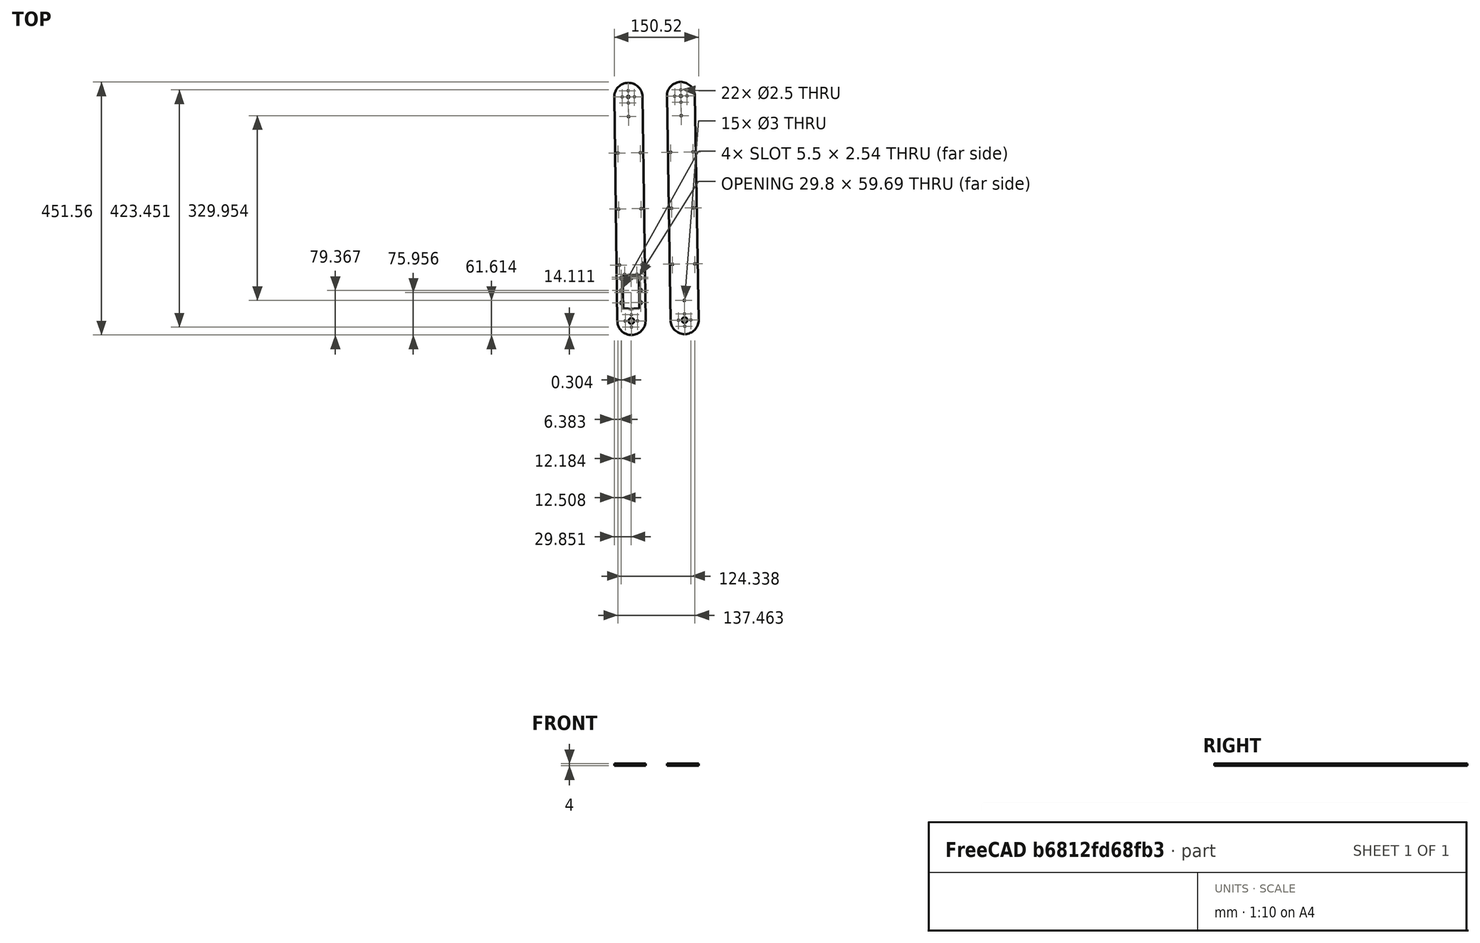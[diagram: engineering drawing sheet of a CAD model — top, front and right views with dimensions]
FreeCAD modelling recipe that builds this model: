
FCSTD DOCUMENT  (FreeCAD 1.0R39109 (Git))
Label: arm_assembly_def2
License: All rights reserved
LicenseURL: https://en.wikipedia.org/wiki/All_rights_reserved
objects: Sketcher::SketchObject×2, PartDesign::Pad×2, PartDesign::Body×2, Assembly::JointGroup×1, Assembly::AssemblyObject×1
note: 12 computed .brp shape members not serialized (recipe doc carries the construction recipe); baked Part::Feature solids carry a one-line shape summary decoded from their .brp

FEATURE [Sketcher::SketchObject] Sketch
  ArcFitTolerance = 1e-06
  AttachmentSupport = -> [XY_Plane]
  FullyConstrained = false
  MakeInternals = false
  MapMode = 5
  sketch-geometry (101):
    g0: LineSegment [constr] StartX=1.5008e-12 StartY=20 StartZ=0 EndX=1.5008e-12 EndY=-20 EndZ=0
    g1: LineSegment [constr] StartX=0 StartY=0 StartZ=0 EndX=0 EndY=400 EndZ=0
    g2: LineSegment [constr] StartX=1.5008e-12 StartY=20 StartZ=0 EndX=1.5008e-12 EndY=25 EndZ=0
    g3: Circle CenterX=0 CenterY=400 CenterZ=0 NormalX=0 NormalY=0 NormalZ=1 AngleXU=0 Radius=2
    g4: Circle CenterX=-10.9997 CenterY=400 CenterZ=0 NormalX=0 NormalY=0 NormalZ=1 AngleXU=0 Radius=1.25
    g5: Circle CenterX=0 CenterY=389 CenterZ=0 NormalX=0 NormalY=0 NormalZ=1 AngleXU=0 Radius=1.25
    g6: Circle CenterX=10.9997 CenterY=400 CenterZ=0 NormalX=0 NormalY=0 NormalZ=1 AngleXU=0 Radius=1.25
    g7: Circle CenterX=0 CenterY=411 CenterZ=0 NormalX=0 NormalY=0 NormalZ=1 AngleXU=0 Radius=1.25
    g8: LineSegment [constr] StartX=0 StartY=-5 StartZ=0 EndX=0 EndY=5.99996 EndZ=0
    g9: Circle [constr] CenterX=0 CenterY=0 CenterZ=0 NormalX=0 NormalY=0 NormalZ=1 AngleXU=0 Radius=14
    g10: LineSegment [constr] StartX=0 StartY=0 StartZ=0 EndX=25.23 EndY=0 EndZ=0
    g11: Circle [constr] CenterX=0 CenterY=-3.8e-05 CenterZ=0 NormalX=0 NormalY=0 NormalZ=1 AngleXU=0 Radius=11
    g12: Circle CenterX=0 CenterY=0 CenterZ=0 NormalX=0 NormalY=0 NormalZ=1 AngleXU=0 Radius=5
    g13: Circle CenterX=10.9997 CenterY=0 CenterZ=0 NormalX=0 NormalY=0 NormalZ=1 AngleXU=0 Radius=1.25
    g14: Circle CenterX=-10.9997 CenterY=0 CenterZ=0 NormalX=0 NormalY=0 NormalZ=1 AngleXU=0 Radius=1.25
    g15: Circle CenterX=0 CenterY=-10.9997 CenterZ=0 NormalX=0 NormalY=0 NormalZ=1 AngleXU=0 Radius=1.25
    g16: Circle CenterX=0 CenterY=11 CenterZ=0 NormalX=0 NormalY=0 NormalZ=1 AngleXU=0 Radius=1.25
    g17: LineSegment [constr] StartX=0 StartY=0 StartZ=0 EndX=-25 EndY=0 EndZ=0
    g18: LineSegment [constr] StartX=20.1368 StartY=86.1 StartZ=0 EndX=20.1368 EndY=25 EndZ=0
    g19: LineSegment [constr] StartX=0.036848 StartY=80.5 StartZ=0 EndX=14.5368 EndY=80.5 EndZ=0
    g20: LineSegment StartX=14.5368 StartY=80.5 StartZ=0 EndX=-14.4632 EndY=80.5 EndZ=0
    g21: LineSegment StartX=14.5368 StartY=80.5 StartZ=0 EndX=14.5368 EndY=25 EndZ=0
    g22: Circle CenterX=11.0368 CenterY=83.3 CenterZ=0 NormalX=0 NormalY=0 NormalZ=1 AngleXU=0 Radius=1.25
    g23: Circle CenterX=17.3368 CenterY=78 CenterZ=0 NormalX=0 NormalY=0 NormalZ=1 AngleXU=0 Radius=1.25
    g24: LineSegment [constr] StartX=-20.0632 StartY=86.1 StartZ=0 EndX=20.1368 EndY=86.1 EndZ=0
    g25: Circle [constr] CenterX=17.3368 CenterY=56.0002 CenterZ=0 NormalX=0 NormalY=0 NormalZ=1 AngleXU=0 Radius=1.25
    g26: Circle [constr] CenterX=17.3368 CenterY=34 CenterZ=0 NormalX=0 NormalY=0 NormalZ=1 AngleXU=0 Radius=1.25
    g27: Circle [constr] CenterX=0.036848 CenterY=38 CenterZ=0 NormalX=0 NormalY=0 NormalZ=1 AngleXU=0 Radius=14
    g28: ArcOfCircle [constr] CenterX=0.036848 CenterY=38 CenterZ=0 NormalX=0 NormalY=0 NormalZ=1 AngleXU=0 Radius=14 StartAngle=4.33214 EndAngle=5.09264
    g29: LineSegment [constr] StartX=5.233 StartY=25 StartZ=0 EndX=14.5368 EndY=25 EndZ=0
    g30: LineSegment [constr] StartX=14.5368 StartY=25 StartZ=0 EndX=20.1368 EndY=25 EndZ=0
    g31: LineSegment [constr] StartX=17.3368 StartY=56.0002 StartZ=0 EndX=-17.2632 EndY=56.0002 EndZ=0
    g32: LineSegment [constr] StartX=-20.0632 StartY=25 StartZ=0 EndX=-20.0632 EndY=86.1 EndZ=0
    g33: LineSegment StartX=-14.4632 StartY=80.5 StartZ=0 EndX=-14.4632 EndY=25 EndZ=0
    g34: Circle CenterX=-17.2632 CenterY=78 CenterZ=0 NormalX=0 NormalY=0 NormalZ=1 AngleXU=0 Radius=1.25
    g35: Circle CenterX=-10.9632 CenterY=83.3 CenterZ=0 NormalX=0 NormalY=0 NormalZ=1 AngleXU=0 Radius=1.25
    g36: Circle [constr] CenterX=-17.2632 CenterY=56.0002 CenterZ=0 NormalX=0 NormalY=0 NormalZ=1 AngleXU=0 Radius=1.25
    g37: Circle [constr] CenterX=-17.2632 CenterY=34 CenterZ=0 NormalX=0 NormalY=0 NormalZ=1 AngleXU=0 Radius=1.25
    g38: LineSegment [constr] StartX=-14.4632 StartY=25 StartZ=0 EndX=-5.15931 EndY=25 EndZ=0
    g39: LineSegment [constr] StartX=-20.0632 StartY=25 StartZ=0 EndX=-14.4632 EndY=25 EndZ=0
    g40: ArcOfCircle CenterX=0.115002 CenterY=3.75548e-06 CenterZ=0 NormalX=0 NormalY=0 NormalZ=1 AngleXU=0 Radius=25.115 StartAngle=3.14159 EndAngle=6.28319
    g41: ArcOfCircle CenterX=0.115002 CenterY=399.959 CenterZ=0 NormalX=0 NormalY=0 NormalZ=1 AngleXU=0 Radius=25.115 StartAngle=0 EndAngle=3.14159
    g42: LineSegment StartX=-25 StartY=3.75548e-06 StartZ=0 EndX=-25 EndY=399.959 EndZ=0
    g43: LineSegment StartX=25.23 StartY=3.75548e-06 StartZ=0 EndX=25.23 EndY=399.959 EndZ=0
    g44: LineSegment [constr] StartX=25.23 StartY=199.98 StartZ=0 EndX=-25 EndY=199.98 EndZ=0
    g45: LineSegment [constr] StartX=25.23 StartY=199.98 StartZ=0 EndX=55.23 EndY=199.98 EndZ=0
    g46: LineSegment [constr] StartX=25.23 StartY=0 StartZ=0 EndX=55.23 EndY=0 EndZ=0
    g47: LineSegment [constr] StartX=55.23 StartY=0 StartZ=0 EndX=55.23 EndY=199.98 EndZ=0
    g48: LineSegment [constr] StartX=55.23 StartY=99.9898 StartZ=0 EndX=25.23 EndY=99.9898 EndZ=0
    g49: LineSegment [constr] StartX=25.23 StartY=99.9898 StartZ=0 EndX=-25 EndY=99.9898 EndZ=0
    g50: LineSegment [constr] StartX=25.23 StartY=399.959 StartZ=0 EndX=55.23 EndY=399.959 EndZ=0
    g51: LineSegment [constr] StartX=55.23 StartY=399.959 StartZ=0 EndX=55.23 EndY=199.98 EndZ=0
    g52: LineSegment [constr] StartX=55.23 StartY=299.969 StartZ=0 EndX=25.23 EndY=299.969 EndZ=0
    g53: LineSegment [constr] StartX=25.23 StartY=299.969 StartZ=0 EndX=-25 EndY=299.969 EndZ=0
    g54: LineSegment [constr] StartX=-25 StartY=299.969 StartZ=0 EndX=-20 EndY=299.969 EndZ=0
    g55: LineSegment [constr] StartX=-20 StartY=299.969 StartZ=0 EndX=-20 EndY=199.98 EndZ=0
    g56: LineSegment [constr] StartX=-20 StartY=199.98 StartZ=0 EndX=-20 EndY=99.9898 EndZ=0
    g57: LineSegment [constr] StartX=25.23 StartY=299.969 StartZ=0 EndX=20.23 EndY=299.969 EndZ=0
    g58: LineSegment [constr] StartX=20.23 StartY=299.969 StartZ=0 EndX=20.23 EndY=199.98 EndZ=0
    g59: LineSegment [constr] StartX=20.23 StartY=199.98 StartZ=0 EndX=20.23 EndY=99.9898 EndZ=0
    g60: Circle CenterX=-20 CenterY=299.969 CenterZ=0 NormalX=0 NormalY=0 NormalZ=1 AngleXU=0 Radius=1.5
    g61: Circle CenterX=20.23 CenterY=299.969 CenterZ=0 NormalX=0 NormalY=0 NormalZ=1 AngleXU=0 Radius=1.5
    g62: Circle CenterX=-20 CenterY=199.98 CenterZ=0 NormalX=0 NormalY=0 NormalZ=1 AngleXU=0 Radius=1.5
    g63: Circle CenterX=20.23 CenterY=199.98 CenterZ=0 NormalX=0 NormalY=0 NormalZ=1 AngleXU=0 Radius=1.5
    g64: Circle CenterX=-20 CenterY=99.9898 CenterZ=0 NormalX=0 NormalY=0 NormalZ=1 AngleXU=0 Radius=1.5
    g65: Circle CenterX=20.23 CenterY=99.9898 CenterZ=0 NormalX=0 NormalY=0 NormalZ=1 AngleXU=0 Radius=1.5
    g66: LineSegment [constr] StartX=-17.2632 StartY=34 StartZ=0 EndX=17.3368 EndY=34 EndZ=0
    g67: LineSegment [constr] StartX=-17.2632 StartY=34 StartZ=0 EndX=-17.2632 EndY=31 EndZ=0
    g68: LineSegment [constr] StartX=17.3368 StartY=34 StartZ=0 EndX=17.3368 EndY=31 EndZ=0
    g69: ArcOfCircle CenterX=-17.2632 CenterY=34 CenterZ=0 NormalX=0 NormalY=0 NormalZ=1 AngleXU=0 Radius=1.25 StartAngle=1.93e-14 EndAngle=3.14159
    g70: ArcOfCircle CenterX=-17.2632 CenterY=31 CenterZ=0 NormalX=0 NormalY=0 NormalZ=1 AngleXU=0 Radius=1.25 StartAngle=3.14159 EndAngle=6.28319
    g71: LineSegment StartX=-16.0132 StartY=34 StartZ=0 EndX=-16.0132 EndY=31 EndZ=0
    g72: LineSegment StartX=-18.5132 StartY=34 StartZ=0 EndX=-18.5132 EndY=31 EndZ=0
    g73: ArcOfCircle CenterX=17.3368 CenterY=34 CenterZ=0 NormalX=0 NormalY=0 NormalZ=1 AngleXU=0 Radius=1.25 StartAngle=1e-16 EndAngle=3.14159
    g74: ArcOfCircle CenterX=17.3368 CenterY=31 CenterZ=0 NormalX=0 NormalY=0 NormalZ=1 AngleXU=0 Radius=1.25 StartAngle=3.14159 EndAngle=6.28319
    g75: LineSegment StartX=18.5868 StartY=34 StartZ=0 EndX=18.5868 EndY=31 EndZ=0
    g76: LineSegment StartX=16.0868 StartY=34 StartZ=0 EndX=16.0868 EndY=31 EndZ=0
    g77: LineSegment [constr] StartX=-17.2632 StartY=78 StartZ=0 EndX=17.3368 EndY=78 EndZ=0
    g78: LineSegment [constr] StartX=-17.2632 StartY=78 StartZ=0 EndX=-17.2632 EndY=75 EndZ=0
    g79: Circle CenterX=-17.2632 CenterY=75 CenterZ=0 NormalX=0 NormalY=0 NormalZ=1 AngleXU=0 Radius=1.25
    g80: LineSegment [constr] StartX=17.3368 StartY=78 StartZ=0 EndX=17.3368 EndY=75 EndZ=0
    g81: Circle CenterX=17.3368 CenterY=75 CenterZ=0 NormalX=0 NormalY=0 NormalZ=1 AngleXU=0 Radius=1.25
    g82: LineSegment StartX=-14.4632 StartY=25 StartZ=0 EndX=-14.4632 EndY=22 EndZ=0
    g83: LineSegment StartX=14.5368 StartY=25 StartZ=0 EndX=14.5368 EndY=22 EndZ=0
    g84: LineSegment StartX=5.233 StartY=22 StartZ=0 EndX=14.5368 EndY=22 EndZ=0
    g85: ArcOfCircle CenterX=0.036848 CenterY=35 CenterZ=0 NormalX=0 NormalY=0 NormalZ=1 AngleXU=0 Radius=14 StartAngle=4.33214 EndAngle=5.09264
    g86: LineSegment StartX=-14.4632 StartY=22 StartZ=0 EndX=-5.15931 EndY=22 EndZ=0
    g87: LineSegment [constr] StartX=-17.2632 StartY=56.0002 StartZ=0 EndX=-17.2632 EndY=53.0002 EndZ=0
    g88: LineSegment [constr] StartX=17.3368 StartY=56.0002 StartZ=0 EndX=17.3368 EndY=53.0002 EndZ=0
    g89: ArcOfCircle CenterX=-17.2632 CenterY=56.0002 CenterZ=0 NormalX=0 NormalY=0 NormalZ=1 AngleXU=0 Radius=1.25 StartAngle=1.93e-14 EndAngle=3.14159
    g90: ArcOfCircle CenterX=-17.2632 CenterY=53.0002 CenterZ=0 NormalX=0 NormalY=0 NormalZ=1 AngleXU=0 Radius=1.25 StartAngle=3.14159 EndAngle=6.28319
    g91: LineSegment StartX=-16.0132 StartY=56.0002 StartZ=0 EndX=-16.0132 EndY=53.0002 EndZ=0
    g92: LineSegment StartX=-18.5132 StartY=56.0002 StartZ=0 EndX=-18.5132 EndY=53.0002 EndZ=0
    g93: ArcOfCircle CenterX=17.3368 CenterY=56.0002 CenterZ=0 NormalX=0 NormalY=0 NormalZ=1 AngleXU=0 Radius=1.25 StartAngle=2.46e-14 EndAngle=3.14159
    g94: ArcOfCircle CenterX=17.3368 CenterY=53.0002 CenterZ=0 NormalX=0 NormalY=0 NormalZ=1 AngleXU=0 Radius=1.25 StartAngle=3.14159 EndAngle=6.28319
    g95: LineSegment StartX=18.5868 StartY=56.0002 StartZ=0 EndX=18.5868 EndY=53.0002 EndZ=0
    g96: LineSegment StartX=16.0868 StartY=56.0002 StartZ=0 EndX=16.0868 EndY=53.0002 EndZ=0
    g97: Circle [constr] CenterX=0.115002 CenterY=399.959 CenterZ=0 NormalX=0 NormalY=0 NormalZ=1 AngleXU=0 Radius=25.115
    g98: LineSegment [constr] StartX=0 StartY=400 StartZ=0 EndX=0 EndY=374.844 EndZ=0
    g99: LineSegment [constr] StartX=0 StartY=374.844 StartZ=0 EndX=0 EndY=364.844 EndZ=0
    g100: Circle CenterX=0 CenterY=364.844 CenterZ=0 NormalX=0 NormalY=0 NormalZ=1 AngleXU=0 Radius=1.5
  constraints (211):
    c: Vertical(g0)
    c: Vertical(g1)
    c: Coincident(g2,g0)
    c: Vertical(g2)
    c: Diameter(g3) = 4
    c: Coincident(g3,g1)
    c: Diameter(g7) = 2.5
    c: Diameter(g4) = 2.5
    c: Diameter(g5) = 2.5
    c: Diameter(g6) = 2.5
    c: Vertical(g8)
    c: Diameter(g9) = 28
    c: Coincident(g17,g9)
    c: Horizontal(g17)
    c: Coincident(g10,g9)
    c: Horizontal(g10)
    c: Diameter(g11) = 22
    c: Diameter(g12) = 10
    c: Coincident(g12,g9)
    c: Diameter(g16) = 2.5
    c: Diameter(g14) = 2.5
    c: Diameter(g15) = 2.5
    c: Diameter(g13) = 2.5
    c: Coincident(g24,g18)
    c: Coincident(g32,g24)
    c: Horizontal(g24)
    c: Vertical(g18)
    c: Vertical(g32)
    c: Distance(g18,g32) = 40.2
    c: Distance(g24,g32) = 61.1
    c: Diameter(g28) = 28
    c: Horizontal(g19)
    c: Coincident(g20,g19)
    c: Horizontal(g20)
    c: Coincident(g33,g20)
    c: Vertical(g33)
    c: Coincident(g21,g19)
    c: Vertical(g21)
    c: Diameter(g22) = 2.5
    c: Equal(g22,g35)
    c: Equal(g22,g26)
    c: Equal(g22,g37)
    c: Equal(g22,g36)
    c: Equal(g22,g34)
    c: Equal(g22,g23)
    c: Equal(g22,g25)
    c: Coincident(g27,g28)
    c: PointOnObject(g28,g27)
    c: Coincident(g29,g28)
    c: Coincident(g29,g21)
    c: Horizontal(g29)
    c: Coincident(g30,g21)
    c: Coincident(g30,g18)
    c: Horizontal(g30)
    c: Coincident(g38,g33)
    c: Coincident(g38,g28)
    c: Horizontal(g38)
    c: Coincident(g39,g32)
    c: Coincident(g39,g33)
    c: Horizontal(g39)
    c: Coincident(g31,g25)
    c: Coincident(g31,g36)
    c: Horizontal(g31)
    c: DistanceY(g27,g1) = 362
    c: Tangent(g40,g42) = 1.5708
    c: Tangent(g40,g43) = -1.5708
    c: Tangent(g41,g42) = 1.5708
    c: Tangent(g41,g43) = -1.5708
    c: Equal(g40,g41)
    c: Symmetric(g43,g43,g44)
    c: Symmetric(g42,g42,g44)
    c: Horizontal(g44)
    c: Distance(g45) = 30
    c: Horizontal(g45)
    c: Coincident(g45,g44)
    c: Distance(g46) = 30
    c: Horizontal(g46)
    c: Coincident(g46,g10)
    c: PointOnObject(g46,g-1)
    c: Coincident(g47,g46)
    c: Coincident(g47,g45)
    c: Vertical(g47)
    c: Symmetric(g47,g47,g48)
    c: PointOnObject(g48,g43)
    c: Horizontal(g48)
    c: Coincident(g49,g48)
    c: PointOnObject(g49,g42)
    c: Horizontal(g49)
    c: Distance(g50) = 30
    c: Horizontal(g50)
    c: Coincident(g50,g41)
    c: Coincident(g51,g50)
    c: Coincident(g51,g45)
    c: Symmetric(g51,g51,g52)
    c: PointOnObject(g52,g43)
    c: Horizontal(g52)
    c: Coincident(g53,g52)
    c: PointOnObject(g53,g42)
    c: Horizontal(g53)
    c: Distance(g54) = 5
    c: Coincident(g54,g53)
    c: PointOnObject(g54,g53)
    c: Coincident(g55,g54)
    c: PointOnObject(g55,g44)
    c: Vertical(g55)
    c: Coincident(g56,g55)
    c: PointOnObject(g56,g49)
    c: Vertical(g56)
    c: Distance(g57) = 5
    c: Coincident(g57,g52)
    c: PointOnObject(g57,g53)
    c: Coincident(g58,g57)
    c: PointOnObject(g58,g44)
    c: Vertical(g58)
    c: Coincident(g59,g58)
    c: PointOnObject(g59,g49)
    c: Vertical(g59)
    c: Coincident(g60,g54)
    c: Diameter(g60) = 3
    c: Coincident(g61,g57)
    c: Equal(g60,g61)
    c: Coincident(g62,g55)
    c: Equal(g60,g62)
    c: Coincident(g63,g58)
    c: Equal(g62,g63)
    c: Coincident(g64,g56)
    c: Equal(g62,g64)
    c: Coincident(g65,g59)
    c: Equal(g64,g65)
    c: DistanceY(g40,g27) = 38
    c: Coincident(g66,g37)
    c: Coincident(g66,g26)
    c: Horizontal(g66)
    c: DistanceX(g66,g66) = 34.6
    c: Distance(g67) = 3
    c: Coincident(g67,g37)
    c: Vertical(g67)
    c: Distance(g68) = 3
    c: Coincident(g68,g26)
    c: Vertical(g68)
    c: Tangent(g69,g71) = 1.5708
    c: Tangent(g69,g72) = -1.5708
    c: Tangent(g70,g71) = 1.5708
    c: Tangent(g70,g72) = -1.5708
    c: Equal(g69,g70)
    c: Radius(g69) = 1.25
    c: Coincident(g69,g37)
    c: Coincident(g70,g67)
    c: Tangent(g73,g75) = 1.5708
    c: Tangent(g73,g76) = -1.5708
    c: Tangent(g74,g75) = 1.5708
    c: Tangent(g74,g76) = -1.5708
    c: Equal(g73,g74)
    c: Coincident(g77,g34)
    c: Coincident(g77,g23)
    c: Horizontal(g77)
    c: DistanceX(g77,g77) = 34.6
    c: Distance(g78) = 3
    c: Coincident(g78,g34)
    c: Vertical(g78)
    c: Coincident(g79,g78)
    c: Equal(g79,g34)
    c: Distance(g80) = 3
    c: Coincident(g80,g23)
    c: Vertical(g80)
    c: Coincident(g81,g80)
    c: Equal(g81,g23)
    c: DistanceX(g33,g21) = 29
    c: Distance(g82) = 3
    c: Coincident(g82,g33)
    c: Vertical(g82)
    c: Distance(g83) = 3
    c: Coincident(g83,g21)
    c: Vertical(g83)
    c: Diameter(g85) = 28
    c: Coincident(g84,g85)
    c: Horizontal(g84)
    c: Coincident(g86,g85)
    c: Horizontal(g86)
    c: DistanceX(g31,g31) = 34.6
    c: Distance(g87) = 3
    c: Coincident(g87,g31)
    c: Vertical(g87)
    c: Distance(g88) = 3
    c: Coincident(g88,g25)
    c: Vertical(g88)
    c: Tangent(g89,g91) = 1.5708
    c: Tangent(g89,g92) = -1.5708
    c: Tangent(g90,g91) = 1.5708
    c: Tangent(g90,g92) = -1.5708
    c: Equal(g89,g90)
    c: Radius(g89) = 1.25
    c: Coincident(g89,g31)
    c: Coincident(g90,g87)
    c: Tangent(g93,g95) = 1.5708
    c: Tangent(g93,g96) = -1.5708
    c: Tangent(g94,g95) = 1.5708
    c: Tangent(g94,g96) = -1.5708
    c: Equal(g93,g94)
    c: Coincident(g97,g41)
    c: PointOnObject(g41,g97)
    c: DistanceX(g1) = 0
    c: DistanceY(g1) = 400
    c: Coincident(g98,g1)
    c: PointOnObject(g98,g97)
    c: Vertical(g98)
    c: Distance(g99) = 10
    c: Coincident(g99,g98)
    c: PointOnObject(g99,g1)
    c: Diameter(g100) = 3
    c: Coincident(g100,g99)
FEATURE [Sketcher::SketchObject] Sketch001
  ArcFitTolerance = 1e-06
  FullyConstrained = false
  MakeInternals = false
  MapMode = 5
  sketch-geometry (47):
    g0: Circle [constr] CenterX=0 CenterY=0.000303 CenterZ=0 NormalX=0 NormalY=0 NormalZ=1 AngleXU=0 Radius=14
    g1: LineSegment [constr] StartX=0 StartY=0.000303 StartZ=0 EndX=0 EndY=400.001 EndZ=0
    g2: Circle CenterX=0 CenterY=400.001 CenterZ=0 NormalX=0 NormalY=0 NormalZ=1 AngleXU=0 Radius=5
    g3: Circle CenterX=0 CenterY=0.000303 CenterZ=0 NormalX=0 NormalY=0 NormalZ=1 AngleXU=0 Radius=2
    g4: Circle [constr] CenterX=0 CenterY=0 CenterZ=0 NormalX=0 NormalY=0 NormalZ=1 AngleXU=0 Radius=11
    g5: ArcOfCircle CenterX=0 CenterY=0 CenterZ=0 NormalX=0 NormalY=0 NormalZ=1 AngleXU=0 Radius=25 StartAngle=3.14159 EndAngle=6.28319
    g6: ArcOfCircle CenterX=0 CenterY=400.001 CenterZ=0 NormalX=0 NormalY=0 NormalZ=1 AngleXU=0 Radius=25 StartAngle=6e-16 EndAngle=3.14159
    g7: LineSegment StartX=-25 StartY=-8e-15 StartZ=0 EndX=-25 EndY=400.001 EndZ=0
    g8: LineSegment StartX=25 StartY=0 StartZ=0 EndX=25 EndY=400.001 EndZ=0
    g9: Circle CenterX=10.9997 CenterY=400.001 CenterZ=0 NormalX=0 NormalY=0 NormalZ=1 AngleXU=0 Radius=1.25
    g10: Circle CenterX=0 CenterY=411.001 CenterZ=0 NormalX=0 NormalY=0 NormalZ=1 AngleXU=0 Radius=1.25
    g11: Circle CenterX=-10.9997 CenterY=400.001 CenterZ=0 NormalX=0 NormalY=0 NormalZ=1 AngleXU=0 Radius=1.25
    g12: Circle CenterX=0 CenterY=389.001 CenterZ=0 NormalX=0 NormalY=0 NormalZ=1 AngleXU=0 Radius=1.25
    g13: Circle CenterX=10.9997 CenterY=0.000303 CenterZ=0 NormalX=0 NormalY=0 NormalZ=1 AngleXU=0 Radius=1.25
    g14: Circle CenterX=0 CenterY=11 CenterZ=0 NormalX=0 NormalY=0 NormalZ=1 AngleXU=0 Radius=1.25
    g15: Circle CenterX=-10.9997 CenterY=0.000303 CenterZ=0 NormalX=0 NormalY=0 NormalZ=1 AngleXU=0 Radius=1.25
    g16: Circle CenterX=0 CenterY=-10.9994 CenterZ=0 NormalX=0 NormalY=0 NormalZ=1 AngleXU=0 Radius=1.25
    g17: LineSegment [constr] StartX=25 StartY=200 StartZ=0 EndX=-25 EndY=200 EndZ=0
    g18: LineSegment [constr] StartX=25 StartY=200 StartZ=0 EndX=55 EndY=200 EndZ=0
    g19: LineSegment [constr] StartX=25 StartY=0 StartZ=0 EndX=55 EndY=0 EndZ=0
    g20: LineSegment [constr] StartX=25 StartY=400.001 StartZ=0 EndX=55 EndY=400.001 EndZ=0
    g21: LineSegment [constr] StartX=55 StartY=200 StartZ=0 EndX=55 EndY=400.001 EndZ=0
    g22: LineSegment [constr] StartX=55 StartY=200 StartZ=0 EndX=55 EndY=0 EndZ=0
    g23: LineSegment [constr] StartX=55 StartY=100 StartZ=0 EndX=25 EndY=100 EndZ=0
    g24: LineSegment [constr] StartX=25 StartY=100 StartZ=0 EndX=-25 EndY=100 EndZ=0
    g25: LineSegment [constr] StartX=55 StartY=300 StartZ=0 EndX=25 EndY=300 EndZ=0
    g26: LineSegment [constr] StartX=25 StartY=300 StartZ=0 EndX=-25 EndY=300 EndZ=0
    g27: LineSegment [constr] StartX=-25 StartY=300 StartZ=0 EndX=-20 EndY=300 EndZ=0
    g28: LineSegment [constr] StartX=-20 StartY=300 StartZ=0 EndX=-20 EndY=200 EndZ=0
    g29: LineSegment [constr] StartX=-20 StartY=200 StartZ=0 EndX=-20 EndY=100 EndZ=0
    g30: LineSegment [constr] StartX=25 StartY=100 StartZ=0 EndX=20 EndY=100 EndZ=0
    g31: LineSegment [constr] StartX=20 StartY=100 StartZ=0 EndX=20 EndY=200 EndZ=0
    g32: LineSegment [constr] StartX=20 StartY=200 StartZ=0 EndX=20 EndY=300 EndZ=0
    g33: Circle CenterX=-20 CenterY=300 CenterZ=0 NormalX=0 NormalY=0 NormalZ=1 AngleXU=0 Radius=1.5
    g34: Circle CenterX=20 CenterY=300 CenterZ=0 NormalX=0 NormalY=0 NormalZ=1 AngleXU=0 Radius=1.5
    g35: Circle CenterX=-20 CenterY=200 CenterZ=0 NormalX=0 NormalY=0 NormalZ=1 AngleXU=0 Radius=1.5
    g36: Circle CenterX=20 CenterY=200 CenterZ=0 NormalX=0 NormalY=0 NormalZ=1 AngleXU=0 Radius=1.5
    g37: Circle CenterX=-20 CenterY=100 CenterZ=0 NormalX=0 NormalY=0 NormalZ=1 AngleXU=0 Radius=1.5
    g38: Circle CenterX=20 CenterY=100 CenterZ=0 NormalX=0 NormalY=0 NormalZ=1 AngleXU=0 Radius=1.5
    g39: Circle [constr] CenterX=0 CenterY=400.001 CenterZ=0 NormalX=0 NormalY=0 NormalZ=1 AngleXU=0 Radius=25
    g40: LineSegment [constr] StartX=0 StartY=400.001 StartZ=0 EndX=0 EndY=375.001 EndZ=0
    g41: LineSegment [constr] StartX=0 StartY=375.001 StartZ=0 EndX=0 EndY=365.001 EndZ=0
    g42: Circle CenterX=0 CenterY=365.001 CenterZ=0 NormalX=0 NormalY=0 NormalZ=1 AngleXU=0 Radius=1.5
    g43: Circle [constr] CenterX=0 CenterY=0 CenterZ=0 NormalX=0 NormalY=0 NormalZ=1 AngleXU=0 Radius=25
    g44: LineSegment [constr] StartX=0 StartY=0 StartZ=0 EndX=0 EndY=25 EndZ=0
    g45: LineSegment [constr] StartX=0 StartY=25 StartZ=0 EndX=0 EndY=35 EndZ=0
    g46: Circle CenterX=0 CenterY=35 CenterZ=0 NormalX=0 NormalY=0 NormalZ=1 AngleXU=0 Radius=1.5
  constraints (103):
    c: Diameter(g0) = 28
    c: Coincident(g1,g0)
    c: Vertical(g1)
    c: Coincident(g2,g1)
    c: Diameter(g3) = 4
    c: Coincident(g3,g0)
    c: Diameter(g4) = 22
    c: Tangent(g5,g7) = 1.5708
    c: Tangent(g5,g8) = -1.5708
    c: Tangent(g6,g7) = 1.5708
    c: Tangent(g6,g8) = -1.5708
    c: Equal(g5,g6)
    c: Radius(g5) = 25
    c: Coincident(g6,g1)
    c: Vertical(g7)
    c: Diameter(g10) = 2.5
    c: Diameter(g11) = 2.5
    c: Diameter(g12) = 2.5
    c: Diameter(g9) = 2.5
    c: Diameter(g14) = 2.5
    c: Diameter(g15) = 2.5
    c: Diameter(g16) = 2.5
    c: Diameter(g13) = 2.5
    c: Symmetric(g8,g8,g17)
    c: Symmetric(g7,g7,g17)
    c: Distance(g18) = 30
    c: Horizontal(g18)
    c: Coincident(g18,g17)
    c: Distance(g19) = 30
    c: Horizontal(g19)
    c: Coincident(g19,g5)
    c: PointOnObject(g19,g-1)
    c: Distance(g20) = 30
    c: Horizontal(g20)
    c: Coincident(g20,g6)
    c: Coincident(g21,g18)
    c: Coincident(g21,g20)
    c: Coincident(g22,g18)
    c: Coincident(g22,g19)
    c: Symmetric(g22,g22,g23)
    c: PointOnObject(g23,g8)
    c: Horizontal(g23)
    c: Coincident(g24,g23)
    c: PointOnObject(g24,g7)
    c: Horizontal(g24)
    c: Symmetric(g21,g21,g25)
    c: PointOnObject(g25,g8)
    c: Horizontal(g25)
    c: Coincident(g26,g25)
    c: PointOnObject(g26,g7)
    c: Horizontal(g26)
    c: Distance(g27) = 5
    c: Horizontal(g27)
    c: Coincident(g27,g26)
    c: Coincident(g28,g27)
    c: PointOnObject(g28,g17)
    c: Vertical(g28)
    c: Coincident(g29,g28)
    c: PointOnObject(g29,g24)
    c: Vertical(g29)
    c: Distance(g30) = 5
    c: Horizontal(g30)
    c: Coincident(g30,g23)
    c: Coincident(g31,g30)
    c: PointOnObject(g31,g17)
    c: Vertical(g31)
    c: Coincident(g32,g31)
    c: PointOnObject(g32,g26)
    c: Vertical(g32)
    c: Diameter(g33) = 3
    c: Coincident(g33,g27)
    c: Coincident(g34,g32)
    c: Equal(g33,g34)
    c: Coincident(g35,g28)
    c: Equal(g33,g35)
    c: Coincident(g36,g31)
    c: Equal(g35,g36)
    c: Coincident(g37,g29)
    c: Equal(g35,g37)
    c: Coincident(g38,g30)
    c: Equal(g37,g38)
    c: DistanceX(g1) = 0
    c: DistanceY(g1) = 400.001
    c: Coincident(g39,g1)
    c: PointOnObject(g6,g39)
    c: Coincident(g40,g1)
    c: PointOnObject(g40,g39)
    c: Vertical(g40)
    c: Distance(g41) = 10
    c: Coincident(g41,g40)
    c: PointOnObject(g41,g1)
    c: Coincident(g43,g5)
    c: PointOnObject(g5,g43)
    c: DistanceX(g4) = 0
    c: DistanceY(g4) = 0
    c: Coincident(g44,g4)
    c: PointOnObject(g44,g43)
    c: Vertical(g44)
    c: Distance(g45) = 10
    c: Coincident(g45,g44)
    c: PointOnObject(g45,g1)
    c: Diameter(g46) = 3
    c: Coincident(g46,g45)
FEATURE [PartDesign::Pad] Pad
  Direction = (0,0,1)
  Length = 4
  Length2 = 10
  Profile = -> Sketch
  ReferenceAxis = -> Sketch [N_Axis]
  Refine = true
  Suppressed = false
  Type = 0
FEATURE [PartDesign::Body] Body  label="arm_low_1"
  AllowCompound = false
  Group = -> [Sketch,Pad]
  Origin = -> Origin
  Placement = pos=(-19.8181,9.93988,17.6558) rot=(0,0,1;0.013804rad)
  Tip = -> Pad
FEATURE [PartDesign::Pad] Pad001
  Direction = (0,0,1)
  Length = 4
  Length2 = 10
  Profile = -> Sketch001
  ReferenceAxis = -> Sketch001 [N_Axis]
  Refine = true
  Suppressed = false
  Type = 0
FEATURE [PartDesign::Body] Body001  label="arm_high_1"
  AllowCompound = false
  Group = -> [Sketch001,Pad001]
  Origin = -> Origin001
  Placement = pos=(68.4839,411.394,17.6558) rot=(0,0,1;3.15834rad)
  Tip = -> Pad001
FEATURE [Assembly::JointGroup] Joints
FEATURE [Assembly::AssemblyObject] Assembly
  Group = -> [Joints]
  Origin = -> Origin003
  Type = Assembly
